# Revit family: TY-B-TY3351_Imperial
name_source: partatom
category: Sprinklers
units: mm (PartAtom-declared; Revit-internal decimal feet)

## family parameters
Always vertical = Yes
Cut with Voids When Loaded = No
Maintain Annotation Orientation = No
OmniClass Number = 23.65.70.17.11.24
OmniClass Title = Fire Fighting Sprinkler Heads
Part Type = Normal
Room Calculation Point = No
Round Connector Dimension = Use Diameter
Shared = No
Work Plane-Based = No

## types (36) — shared parameters
COBie = Yes
COBie.Component.Name = Sprinklers:Sidewall_SIN
COBie.Type = Yes
COBie.Type.AssetType = Fixed
COBie.Type.Category = Pr_70_55_97_84:Sprinklers
COBie.Type.DurationUnit = year
COBie.Type.Manufacturer = Tyco Fire Protection Products
COBie.Type.Material = Bronze
COBie.Type.NominalHeight = 0' - 0"
COBie.Type.NominalLength = 0' - 0"
COBie.Type.NominalWidth = 0' - 0"
COBie.Type.Shape = Cylinder
COBie.Type.Size = 1/2"(DN15)
COBie.Type.WarrantyGuarantorParts = http://tycofsbp.com
Coverage = Standard
Coverage_ = Standard
Default Elevation = 0' - 0"
K-Factor = 5.5493
Manufacturer = Tyco Fire Protection Products
Manufacturer URL = www.tyco-fire.com
Material_ = Bronze
Model = TY-B
Nominal Diameter 1 = 1"
Orifice = Standard
Orifice Size = 0"
Outside Diameter 1 = 1"
Response = Standard
SIN No = TY3351
Takeout 1 = 2"
Technical Data Sheet No = TFP161
zero-valued in all types: COBie.Type.ReplacementCost, Style Id

## per-type parameters (varying)
| type | COBie.Component.Description | COBie.Type.Colour | COBie.Type.Finish | COBie.Type.ModelNumber | COBie.Type.ModelReference | Description | Finish_ | Part No | Response_ | Temperature Rating |
| Horizontal Sidewall Brass 135°F/57°C 5.6K ½"(DN15) NPT_57-578-1-135 | TY-B Wet Sidewall  57.2°C K80 DN15 NPT Br | Yellow | Natural Brass | 57-578-1-135 | TY-B Wet Sidewall  57.2°C K80 DN15 NPT Br | TY-B Horizontal Sidewall Brass 135°F/57°C 5.6K ½" NPT | Natural Brass | 57-578-1-135 | Standard | 135 °F |
| Horizontal Sidewall Brass 155°F/68°C 5.6K ½"(DN15) NPT_57-578-1-155 | TY-B Wet Sidewall  68.3°C K80 DN15 NPT Br | Yellow | Natural Brass | 57-578-1-155 | TY-B Wet Sidewall  68.3°C K80 DN15 NPT Br | TY-B Horizontal Sidewall Brass 155°F/68°C 5.6K ½" NPT | Natural Brass | 57-578-1-155 | Standard | 155 °F |
| Horizontal Sidewall Brass 175°F/79°C 5.6K ½"(DN15) NPT_57-578-1-175 | TY-B Wet Sidewall  79.4°C K80 DN15 NPT Br | Yellow | Natural Brass | 57-578-1-175 | TY-B Wet Sidewall  79.4°C K80 DN15 NPT Br | TY-B Horizontal Sidewall Brass 175°F/79°C 5.6K ½" NPT | Natural Brass | 57-578-1-175 | Standard | 175 °F |
| Horizontal Sidewall Brass 200°F/93°C 5.6K ½"(DN15) NPT_57-578-1-200 | TY-B Wet Sidewall  93.3°C K80 DN15 NPT Br | Yellow | natural Brass | 57-578-1-200 | TY-B Wet Sidewall  93.3°C K80 DN15 NPT Br | TY-B Horizontal Sidewall Brass 200°F/93°C 5.6K ½" NPT | Natural Brass | 57-578-1-200 | Standard | 200 °F |
| Horizontal Sidewall Brass 286°F/141°C 5.6K ½"(DN15) NPT_57-578-1-286 | TY-B Wet Sidewall  141.1°C K80 DN15 NPT Br | Yellow | Natural Brass | 57-578-1-286 | TY-B Wet Sidewall  141.1°C K80 DN15 NPT Br | TY-B Horizontal Sidewall Brass 286°F/141°C 5.6K ½" NPT | Natural Brass | 57-578-1-286 | Standard | 286 °F |
| Horizontal Sidewall Brass 360°F/182°C 5.6K ½"(DN15) NPT_57-578-1-360 | TY-B Wet Sidewall  182.2°C K80 DN15 NPT Br | Yellow | Natural Brass | 57-578-1-360 | TY-B Wet Sidewall  182.2°C K80 DN15 NPT Br | TY-B Horizontal Sidewall Brass 360°F/182°C 5.6K ½" NPT | Natural Brass | 57-578-1-360 | Standard | 360 °F |
| Horizontal Sidewall White 135°F/57°C 5.6K ½"(DN15) NPT_57-578-4-135 | TY-B Wet Sidewall  57.2°C K80 DN15 NPT Wh9003 | White | Signal White | 57-578-4-135 | TY-B Wet Sidewall  57.2°C K80 DN15 NPT Wh9003 | TY-B Horizontal Sidewall White 135°F/57°C 5.6K ½" NPT | White RAL9003 | 57-578-4-135 | Standard | 135 °F |
| Horizontal Sidewall White 155°F/68°C 5.6K ½"(DN15) NPT_57-578-4-155 | TY-B Wet Sidewall  68.3°C K80 DN15 NPT Wh9003 | White | Signal White | 57-578-4-155 | TY-B Wet Sidewall  68.3°C K80 DN15 NPT Wh9003 | TY-B Horizontal Sidewall White 155°F/68°C 5.6K ½" NPT | White RAL9003 | 57-578-4-155 | Standard | 155 °F |
| Horizontal Sidewall White 175°F/79°C 5.6K ½"(DN15) NPT_57-578-4-175 | TY-B Wet Sidewall  79.4°C K80 DN15 NPT Wh9003 | White | Signal White | 57-578-4-175 | TY-B Wet Sidewall  79.4°C K80 DN15 NPT Wh9003 | TY-B Horizontal Sidewall White 175°F/79°C 5.6K ½" NPT | White RAL9003 | 57-578-4-175 | Standard | 175 °F |
| Horizontal Sidewall White 200°F/93°C 5.6K ½"(DN15) NPT_57-578-4-200 | TY-B Wet Sidewall  93.3°C K80 DN15 NPT Wh9003 | White | Signal White | 57-578-4-200 | TY-B Wet Sidewall  93.3°C K80 DN15 NPT Wh9003 | TY-B Horizontal Sidewall White 200°F/93°C 5.6K ½" NPT | White RAL9003 | 57-578-4-200 | Standard | 200 °F |
| Horizontal Sidewall White 286°F/141°C 5.6K ½"(DN15) NPT_57-578-4-286 | TY-B Wet Sidewall  141.1°C K80 DN15 NPT Wh9003 | White | Signal White | 57-578-4-286 | TY-B Wet Sidewall  141.1°C K80 DN15 NPT Wh9003 | TY-B Horizontal Sidewall White 286°F/141°C 5.6K ½" NPT | White RAL9003 | 57-578-4-286 | Standrad | 286 °F |
| Horizontal Sidewall White 360°F/182°C 5.6K ½"(DN15) NPT_57-578-4-360 | TY-B Wet Sidewall  182.2°C K80 DN15 NPT Wh9003 | White | Signal White | 57-578-4-360 | TY-B Wet Sidewall  182.2°C K80 DN15 NPT Wh9003 | TY-B Horizontal Sidewall White 360°F/182°C 5.6K ½" NPT | White RAL9003 | 57-578-4-360 | Standard | 360 °F |
| Horizontal Sidewall JetBlack 155°F/68°C 5.6K ½"(DN15) NPT_57-578-5-155 | TY-B Wet Sidewall  68.3°C K80 DN15 NPT JBlk | Black | Jet Black | 57-578-5-155 | TY-B Wet Sidewall  68.3°C K80 DN15 NPT JBlk | TY-B Horizontal Sidewall JetBlack 155°F/68°C 5.6K ½" NPT | Jet Black RAL9005 | 57-578-5-155 | Standard | 155 °F |
| Horizontal Sidewall JetBlack 200°F/93°C 5.6K ½"(DN15) NPT_57-578-5-200 | TY-B Wet Sidewall  93.3°C K80 DN15 NPT JBlk | Black | Jet Black | 57-578-5-200 | TY-B Wet Sidewall  93.3°C K80 DN15 NPT JBlk | TY-B Horizontal Sidewall JetBlack 200°F/93°C 5.6K ½" NPT | Jet Black RAL9005 | 57-578-5-200 | Standard | 200 °F |
| Horizontal Sidewall Wax 135°F/57°C 5.6K ½"(DN15) NPT_57-578-6-135 | TY-B Wet Sidewall  57.2°C K80 DN15 NPT Wx | Gray | Wax Coated | 57-578-6-135 | TY-B Wet Sidewall  57.2°C K80 DN15 NPT Wx | TY-B Horizontal Sidewall Wax 135°F/57°C 5.6K ½" NPT | Wax Coated | 57-578-6-135 | Standard | 135 °F |
| Horizontal Sidewall Wax 155°F/68°C 5.6K ½"(DN15) NPT_57-578-6-155 | TY-B Wet Sidewall  68.3°C K80 DN15 NPT Wx | Gray | Wax Coated | 57-578-6-155 | TY-B Wet Sidewall  68.3°C K80 DN15 NPT Wx | TY-B Horizontal Sidewall Wax 155°F/68°C 5.6K ½" NPT | Wax Coated | 57-578-6-155 | Standard | 155 °F |
| Horizontal Sidewall Wax 175°F/79°C 5.6K ½"(DN15) NPT_57-578-6-175 | TY-B Wet Sidewall  79.4°C K80 DN15 NPT Wx | Gray | Wax Coated | 57-578-6-175 | TY-B Wet Sidewall  79.4°C K80 DN15 NPT Wx | TY-B Horizontal Sidewall Wax 175°F/79°C 5.6K ½" NPT | Wax Coated | 57-578-6-175 | Standard | 175 °F |
| Horizontal Sidewall Wax 200°F/93°C 5.6K ½"(DN15) NPT_57-578-6-200 | TY-B Wet Sidewall  93.3°C K80 DN15 NPT Wx | Gray | Wax Coated | 57-578-6-200 | TY-B Wet Sidewall  93.3°C K80 DN15 NPT Wx | TY-B Horizontal Sidewall Wax 200°F/93°C 5.6K ½" NPT | Wax Coated | 57-578-6-200 | Standard | 200 °F |
| Horizontal Sidewall Wax 286°F/141°C 5.6K ½"(DN15) NPT_57-578-6-286 | TY-B Wet Sidewall  141.1°C K80 DN15 NPT Wx | Gray | Wax Coated | 57-578-6-286 | TY-B Wet Sidewall  141.1°C K80 DN15 NPT Wx | TY-B Horizontal Sidewall Wax 286°F/141°C 5.6K ½" NPT | Wax Coated | 57-578-6-286 | Standard | 286 °F |
| Horizontal Sidewall Lead 135°F/57°C 5.6K ½"(DN15) NPT_57-578-7-135 | TY-B Wet Sidewall  57.2°C K80 DN15 NPT Lead | Gray | Lead Coated | 57-578-7-135 | TY-B Wet Sidewall  57.2°C K80 DN15 NPT Lead | TY-B Horizontal Sidewall Lead 135°F/57°C 5.6K ½" NPT | Lead Coated | 57-578-7-135 | Standard | 135 °F |
| Horizontal Sidewall Lead 155°F/68°C 5.6K ½"(DN15) NPT_57-578-7-155 | TY-B Wet Sidewall  68.3°C K80 DN15 NPT Lead | Gray | Lead Coated | 57-578-7-155 | TY-B Wet Sidewall  68.3°C K80 DN15 NPT Lead | TY-B Horizontal Sidewall Lead 155°F/68°C 5.6K ½" NPT | Lead Coated | 57-578-7-155 | Standard | 155 °F |
| Horizontal Sidewall Lead 175°F/79°C 5.6K ½"(DN15) NPT_57-578-7-175 | TY-B Wet Sidewall  79.4°C K80 DN15 NPT Lead | Gray | Lead Coated | 57-578-7-175 | TY-B Wet Sidewall  79.4°C K80 DN15 NPT Lead | TY-B Horizontal Sidewall Lead 175°F/79°C 5.6K ½" NPT | Lead Coated | 57-578-7-175 | Standard | 175 °F |
| Horizontal Sidewall Lead 200°F/93°C 5.6K ½"(DN15) NPT_57-578-7-200 | TY-B Wet Sidewall  93.3°C K80 DN15 NPT Lead | Gray | Lead Coated | 57-578-7-200 | TY-B Wet Sidewall  93.3°C K80 DN15 NPT Lead | TY-B Horizontal Sidewall Lead 200°F/93°C 5.6K ½" NPT | Lead Coated | 57-578-7-200 | Standard | 200 °F |
| Horizontal Sidewall Lead 286°F/141°C 5.6K ½"(DN15) NPT_57-578-7-286 | TY-B Wet Sidewall  141.1°C K80 DN15 NPT Lead | Gray | Lead Coated | 57-578-7-286 | TY-B Wet Sidewall  141.1°C K80 DN15 NPT Lead | TY-B Horizontal Sidewall Lead 286°F/141°C 5.6K ½" NPT | Lead Coated | 57-578-7-286 | Standard | 286 °F |
| Horizontal Sidewall Lead 360°F/182°C 5.6K ½"(DN15) NPT_57-578-7-360 | TY-B Wet Sidewall  182.2°C K80 DN15 NPT Lead | Gray | Lead Coated | 57-578-7-360 | TY-B Wet Sidewall  182.2°C K80 DN15 NPT Lead | TY-B Horizontal Sidewall Lead 360°F/182°C 5.6K ½" NPT | Lead Coated | 57-578-7-360 | Standard | 360 °F |
| Horizontal Sidewall Wax Over Lead 135°F/57°C 5.6K ½"(DN15) NPT_57-578-8-135 | TY-B Wet Sidewall  57.2°C K80 DN15 NPT WoL | Gray | Wax Over Coated | 57-578-8-135 | TY-B Wet Sidewall  57.2°C K80 DN15 NPT WoL | TY-B Horizontal Sidewall Wax Over Lead 135°F/57°C 5.6K ½" NPT | Wax Over Lead | 57-578-8-135 | Standard | 135 °F |
| Horizontal Sidewall Wax Over Lead 155°F/68°C 5.6K ½"(DN15) NPT_57-578-8-155 | TY-B Wet Sidewall  68.3°C K80 DN15 NPT WoL | Gray | Wax Over Coated | 57-578-8-155 | TY-B Wet Sidewall  68.3°C K80 DN15 NPT WoL | TY-B Horizontal Sidewall Wax Over Lead 155°F/68°C 5.6K ½" NPT | Wax Over Lead | 57-578-8-155 | Standard | 155 °F |
| Horizontal Sidewall Wax Over Lead 175°F/79°C 5.6K ½"(DN15) NPT_57-578-8-175 | TY-B Wet Sidewall  79.4°C K80 DN15 NPT WoL | Gray | Wax Over Coated | 57-578-8-175 | TY-B Wet Sidewall  79.4°C K80 DN15 NPT WoL | TY-B Horizontal Sidewall Wax Over Lead 175°F/79°C 5.6K ½" NPT | Wax Over Lead | 57-578-8-175 | Standard | 175 °F |
| Horizontal Sidewall Wax Over Lead 200°F/93°C 5.6K ½"(DN15) NPT_57-578-8-200 | TY-B Wet Sidewall  93.3°C K80 DN15 NPT WoL | Gray | Wax Over Coated | 57-578-8-200 | TY-B Wet Sidewall  93.3°C K80 DN15 NPT WoL | TY-B Horizontal Sidewall Wax Over Lead 200°F/93°C 5.6K ½" NPT | Wax Over Lead | 57-578-8-200 | Standard | 200 °F |
| Horizontal Sidewall Wax Over Lead 286°F/141°C 5.6K ½"(DN15) NPT_57-578-8-286 | TY-B Wet Sidewall  141.1°C K80 DN15 NPT WoL | Gray | Wax Over Coated | 57-578-8-286 | TY-B Wet Sidewall  141.1°C K80 DN15 NPT WoL | TY-B Horizontal Sidewall Wax Over Lead 286°F/141°C 5.6K ½" NPT | Wax Over Lead | 57-578-8-286 | Standard | 286 °F |
| Horizontal Sidewall Chrome 135°F/57°C 5.6K ½"(DN15) NPT_57-578-9-135 | TY-B Wet Sidewall  57.2°C K80 DN15 NPT Chr | Gray | Wax Over Coated | 57-578-9-135 | TY-B Wet Sidewall  57.2°C K80 DN15 NPT Chr | TY-B Horizontal Sidewall Chrome 135°F/57°C 5.6K ½" NPT | Chrome Plated | 57-578-9-135 | Standard | 135 °F |
| Horizontal Sidewall Chrome 155°F/68°C 5.6K ½"(DN15) NPT_57-578-9-155 | TY-B Wet Sidewall  68.3°C K80 DN15 NPT Chr | Silver | Chrome Plated | 57-578-9-155 | TY-B Wet Sidewall  68.3°C K80 DN15 NPT Chr | TY-B Horizontal Sidewall Chrome 155°F/68°C 5.6K ½" NPT | Chrome Plated | 57-578-9-155 | Standard | 155 °F |
| Horizontal Sidewall Chrome 175°F/79°C 5.6K ½"(DN15) NPT_57-578-9-175 | TY-B Wet Sidewall  79.4°C K80 DN15 NPT Chr | Silver | Chrome Plated | 57-578-9-175 | TY-B Wet Sidewall  79.4°C K80 DN15 NPT Chr | TY-B Horizontal Sidewall Chrome 175°F/79°C 5.6K ½" NPT | Chrome Plated | 57-578-9-175 | Standard | 175 °F |
| Horizontal Sidewall Chrome 200°F/93°C 5.6K ½"(DN15) NPT_57-578-9-200 | TY-B Wet Sidewall  93.3°C K80 DN15 NPT Chr | Silver | Chrome Plated | 57-578-9-200 | TY-B Wet Sidewall  93.3°C K80 DN15 NPT Chr | TY-B Horizontal Sidewall Chrome 200°F/93°C 5.6K ½" NPT | Chrome Plated | 57-578-9-200 | Standard | 200 °F |
| Horizontal Sidewall Chrome 286°F/141°C 5.6K ½"(DN15) NPT_57-578-9-286 | TY-B Wet Sidewall  141.1°C K80 DN15 NPT Chr | Silver | Chrome Plated | 57-578-9-286 | TY-B Wet Sidewall  141.1°C K80 DN15 NPT Chr | TY-B Horizontal Sidewall Chrome 286°F/141°C 5.6K ½" NPT | Chrome Plated | 57-578-9-286 | Standard | 286 °F |
| Horizontal Sidewall Chrome 360°F/182°C 5.6K ½"(DN15) NPT_57-578-9-360 | TY-B Wet Sidewall  182.2°C K80 DN15 NPT Chr | Silver | Chrome Plated | 57-578-9-360 | TY-B Wet Sidewall  182.2°C K80 DN15 NPT Chr | TY-B Horizontal Sidewall Chrome 360°F/182°C 5.6K ½" NPT | Chrome Plated | 57-578-9-360 | Standard | 360 °F |

## geometry (parser evidence)
native form markers: Blend x2, Sweep x51
no freeform markers — native parametric forms only
